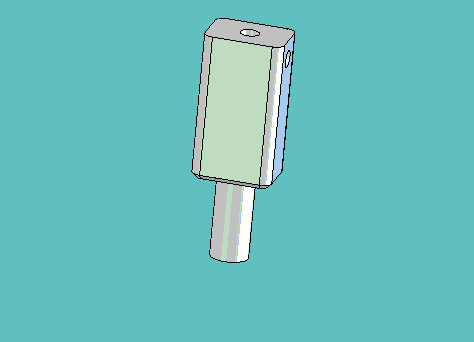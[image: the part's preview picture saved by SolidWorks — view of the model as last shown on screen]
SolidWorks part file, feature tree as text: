
SOLIDWORKS PART (.sldprt)
format: sldprt  version: not decoded by parser v0  size: 406,016 bytes
history: native  units: mm
features: sketch x5, cut_extrude x2, material x1, revolve x1, extrude x1, fillet x1, chamfer x1 (+11 scaffold rows collapsed)
feature tree (23):
  scaffold x11  (default folders/planes/origin — collapsed)
  material  "Material <not specified>"
  sketch  "Sketch1"  dims[D1=~23.41245mm D2=9.525mm D3=6.0452mm D4=36.5125mm]
  revolve  "Revolve1"  Angle=360deg
  sketch  "Sketch5"  dims[D3=12.7mm D1=4.7625mm D2=4.7625mm]
  extrude  "Extrude1"  [1 undecoded]
  sketch  "Sketch3"  dims[D1=3.048mm]
  cut_extrude  "Cut-Extrude2"  Depth=9.525mm
  sketch  "Sketch4"  dims[D2=2.7051mm D1=3.175mm]
  cut_extrude  "Cut-Extrude3"  [1 undecoded]
  sketch  "Sketch2"  dims[D1=~5.58546mm]
  fillet  "Fillet1"  Radius=1.5875mm
  chamfer  "Chamfer1"  Distance=0.762mm Angle=45deg
decode coverage: 9 of 11 modeling features carry decoded parameters
note: ~ marks probable driven/reference dimensions
note: 2 parameter values undecoded
note: suppression state not decoded; provenance and decode notes live in map.json
